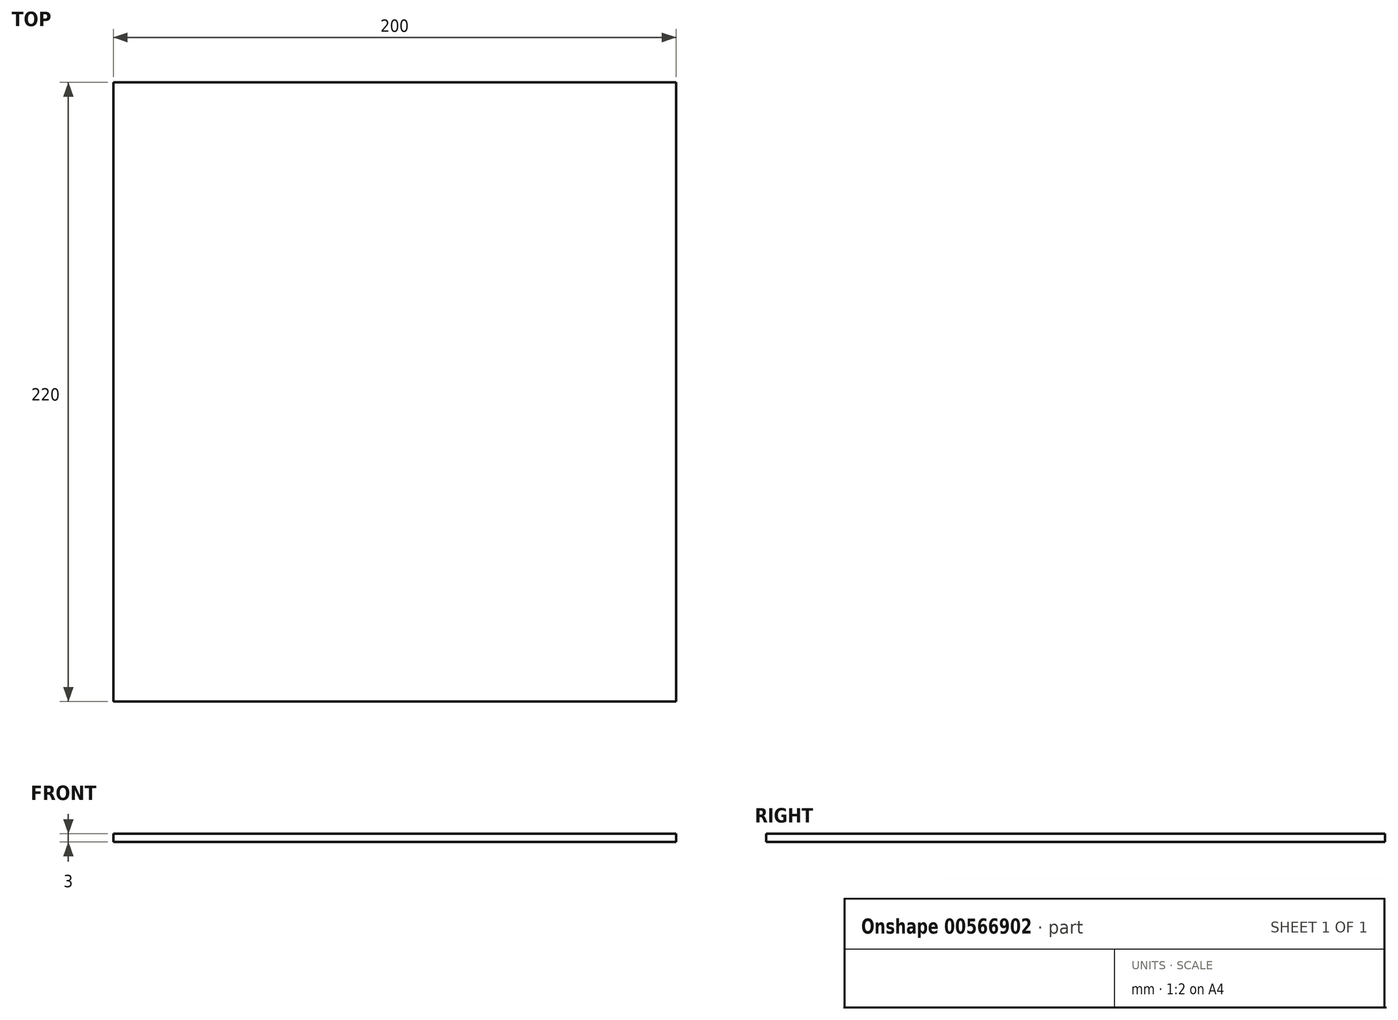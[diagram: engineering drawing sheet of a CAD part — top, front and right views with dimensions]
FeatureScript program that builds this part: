
annotation { "Feature Type Name" : "Feature", "Feature Type Description" : "" }
export const myFeature = defineFeature(function(context is Context, id is Id, definition is map)
    precondition{}
    {
        {
            var Q0;
            Q0=qCreatedBy(makeId("Top.planeOp"),FACE);
            var sketch = newSketch(context, id + "F0", { "sketchPlane" : qUnion([Q0])});
            skLineSegment(sketch, "E0.bottom", {"start": v(-134.5, 165.93) * mm, "end": v(65.5, 165.93) * mm});
            skLineSegment(sketch, "E0.top", {"start": v(-134.5, -54.07) * mm, "end": v(65.5, -54.07) * mm});
            skLineSegment(sketch, "E0.left", {"start": v(-134.5, 165.93) * mm, "end": v(-134.5, -54.07) * mm});
            skLineSegment(sketch, "E0.right", {"start": v(65.5, 165.93) * mm, "end": v(65.5, -54.07) * mm});
            skSolve(sketch);
        }
        {
            var Q0;
            Q0=makeQuery(id+"F0.imprint","IMPRINT",FACE,{"disambiguationData":[TD([[makeQuery(id+"F0.imprint","IMPRINT",EDGE,{"derivedFrom":sQuery(id+"F0.wireOp",EDGE,"E0.bottom")}),-1.0]])]});
            extrude(context, id + "F1", {"entities" : qUnion([Q0]), "depth" : 3 * mm, "offsetDistance" : 25 * mm});
        }
    });
